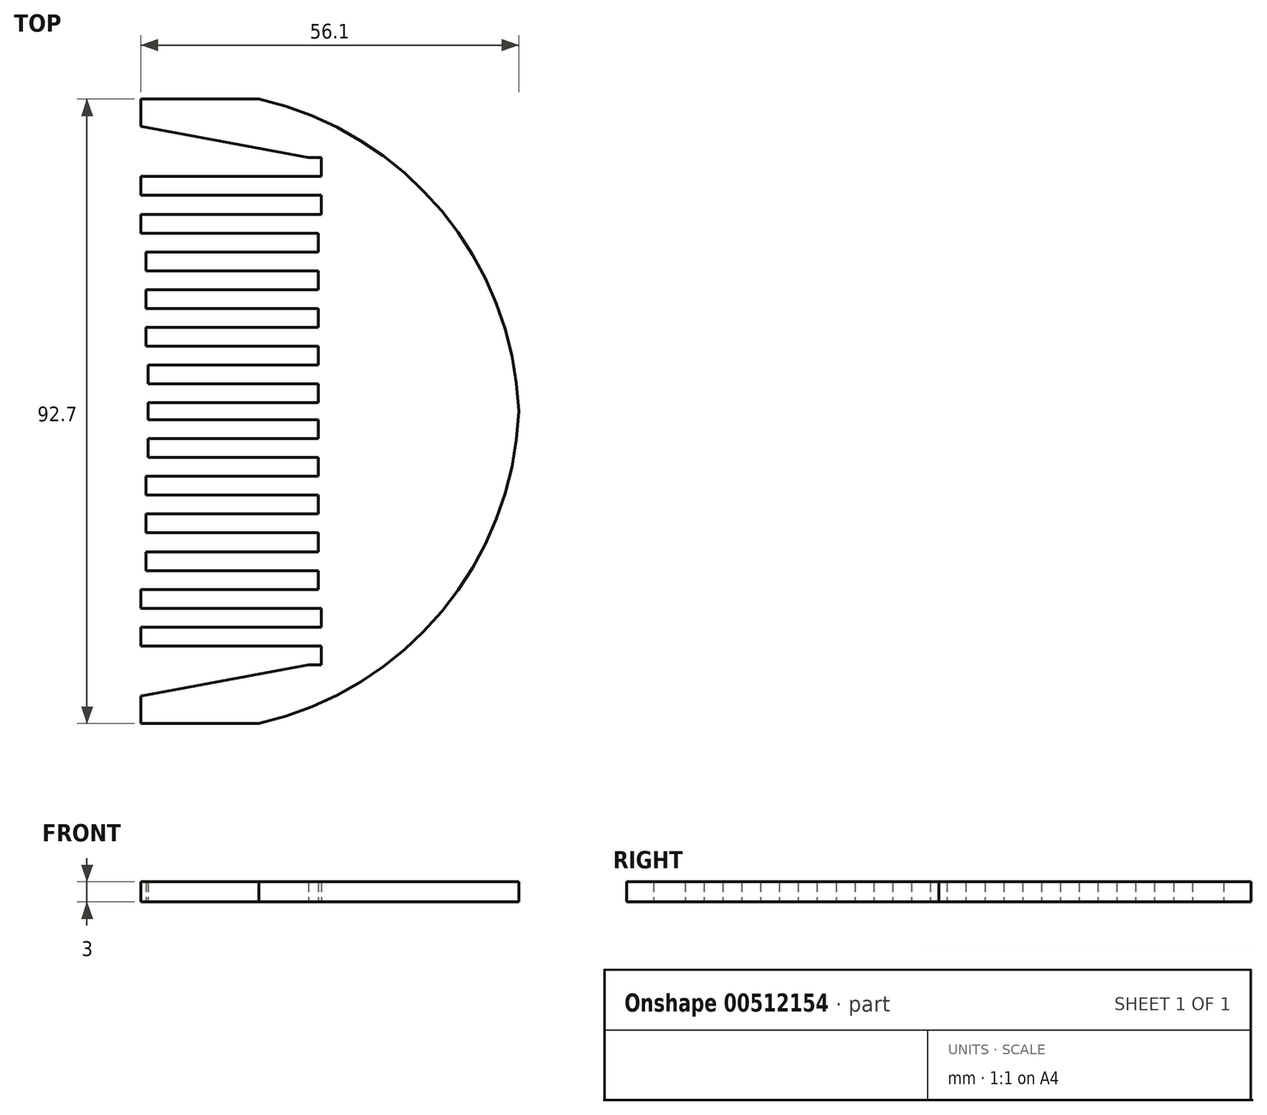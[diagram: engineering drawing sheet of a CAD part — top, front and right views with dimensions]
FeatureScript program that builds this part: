
annotation { "Feature Type Name" : "Feature", "Feature Type Description" : "" }
export const myFeature = defineFeature(function(context is Context, id is Id, definition is map)
    precondition{}
    {
        {
            var Q0;
            Q0=qCreatedBy(makeId("Top.planeOp"),FACE);
            var sketch = newSketch(context, id + "F0", { "sketchPlane" : qUnion([Q0])});
            skLineSegment(sketch, "E0", {"start": v(-57.4, 0) * mm, "end": v(-57.4, -4.05) * mm});
            skLineSegment(sketch, "E1", {"start": v(-57.4, -4.05) * mm, "end": v(-32.5, -8.7) * mm});
            skLineSegment(sketch, "E2", {"start": v(-32.5, -8.7) * mm, "end": v(-30.6, -8.7) * mm});
            skLineSegment(sketch, "E3", {"start": v(-30.6, -8.7) * mm, "end": v(-30.6, -11.5) * mm});
            skLineSegment(sketch, "E4", {"start": v(-30.6, -11.5) * mm, "end": v(-57.4, -11.5) * mm});
            skLineSegment(sketch, "E5", {"start": v(-57.4, -11.5) * mm, "end": v(-57.4, -14.3) * mm});
            skLineSegment(sketch, "E6", {"start": v(-57.4, -14.3) * mm, "end": v(-30.6, -14.3) * mm});
            skLineSegment(sketch, "E7", {"start": v(-30.6, -14.3) * mm, "end": v(-30.6, -17.1) * mm});
            skLineSegment(sketch, "E8", {"start": v(-30.6, -17.1) * mm, "end": v(-57.4, -17.1) * mm});
            skLineSegment(sketch, "E9", {"start": v(-57.4, -17.1) * mm, "end": v(-57.4, -19.9) * mm});
            skLineSegment(sketch, "E10", {"start": v(-57.4, -19.9) * mm, "end": v(-31.06, -19.9) * mm});
            skLineSegment(sketch, "E11", {"start": v(-31.06, -19.9) * mm, "end": v(-31.06, -22.7) * mm});
            skLineSegment(sketch, "E12", {"start": v(-31.06, -22.7) * mm, "end": v(-56.63, -22.7) * mm});
            skLineSegment(sketch, "E13", {"start": v(-56.63, -22.7) * mm, "end": v(-56.63, -25.5) * mm});
            skLineSegment(sketch, "E14", {"start": v(-56.63, -25.5) * mm, "end": v(-31.06, -25.5) * mm});
            skLineSegment(sketch, "E15", {"start": v(-31.06, -25.5) * mm, "end": v(-31.06, -28.3) * mm});
            skLineSegment(sketch, "E16", {"start": v(-31.06, -28.3) * mm, "end": v(-56.63, -28.3) * mm});
            skLineSegment(sketch, "E17", {"start": v(-56.63, -28.3) * mm, "end": v(-56.63, -31.1) * mm});
            skLineSegment(sketch, "E18", {"start": v(-56.63, -31.1) * mm, "end": v(-31.06, -31.1) * mm});
            skLineSegment(sketch, "E19", {"start": v(-31.06, -31.1) * mm, "end": v(-31.06, -33.9) * mm});
            skLineSegment(sketch, "E20", {"start": v(-31.06, -33.9) * mm, "end": v(-56.63, -33.9) * mm});
            skLineSegment(sketch, "E21", {"start": v(-56.63, -33.9) * mm, "end": v(-56.63, -36.7) * mm});
            skLineSegment(sketch, "E22", {"start": v(-56.63, -36.7) * mm, "end": v(-31.06, -36.7) * mm});
            skLineSegment(sketch, "E23", {"start": v(-31.06, -36.7) * mm, "end": v(-31.06, -39.5) * mm});
            skLineSegment(sketch, "E24", {"start": v(-31.06, -39.5) * mm, "end": v(-56.34, -39.5) * mm});
            skLineSegment(sketch, "E25", {"start": v(-56.34, -39.5) * mm, "end": v(-56.34, -42.3) * mm});
            skLineSegment(sketch, "E26", {"start": v(-56.34, -42.3) * mm, "end": v(-31.06, -42.3) * mm});
            skLineSegment(sketch, "E27", {"start": v(-31.06, -42.3) * mm, "end": v(-31.06, -45.1) * mm});
            skLineSegment(sketch, "E28", {"start": v(-31.06, -45.1) * mm, "end": v(-56.34, -45.1) * mm});
            skLineSegment(sketch, "E29", {"start": v(-56.34, -45.1) * mm, "end": v(-56.34, -46.35) * mm});
            skLineSegment(sketch, "E30", {"start": v(-56.34, -46.35) * mm, "end": v(-1.3, -46.35) * mm, "construction": true});
            skLineSegment(sketch, "E31", {"start": v(-57.4, 0) * mm, "end": v(-39.9, 0) * mm});
            skArc(sketch, "E32", {"start": v(-1.3, -46.35) * mm, "mid": v(-12.74, -16.63) * mm, "end": v(-39.9, 0) * mm});
            skLineSegment(sketch, "E33.MirrorCS", {"start": v(-57.4, -92.7) * mm, "end": v(-57.4, -88.66) * mm});
            skLineSegment(sketch, "E34.MirrorCS", {"start": v(-56.34, -47.6) * mm, "end": v(-56.34, -46.35) * mm});
            skLineSegment(sketch, "E35.MirrorCS", {"start": v(-56.63, -70) * mm, "end": v(-56.63, -67.2) * mm});
            skLineSegment(sketch, "E36.MirrorCS", {"start": v(-30.6, -78.4) * mm, "end": v(-30.6, -75.6) * mm});
            skLineSegment(sketch, "E37.MirrorCS", {"start": v(-31.06, -67.2) * mm, "end": v(-31.06, -64.4) * mm});
            skLineSegment(sketch, "E38.MirrorCS", {"start": v(-56.63, -64.4) * mm, "end": v(-56.63, -61.6) * mm});
            skLineSegment(sketch, "E39.MirrorCS", {"start": v(-56.34, -53.2) * mm, "end": v(-56.34, -50.4) * mm});
            skLineSegment(sketch, "E40.MirrorCS", {"start": v(-56.63, -58.8) * mm, "end": v(-56.63, -56) * mm});
            skLineSegment(sketch, "E41.MirrorCS", {"start": v(-31.06, -61.6) * mm, "end": v(-31.06, -58.8) * mm});
            skLineSegment(sketch, "E42.MirrorCS", {"start": v(-31.06, -56) * mm, "end": v(-31.06, -53.2) * mm});
            skLineSegment(sketch, "E43.MirrorCS", {"start": v(-32.5, -84) * mm, "end": v(-30.6, -84) * mm});
            skLineSegment(sketch, "E44.MirrorCS", {"start": v(-57.4, -81.2) * mm, "end": v(-57.4, -78.4) * mm});
            skLineSegment(sketch, "E45.MirrorCS", {"start": v(-31.06, -50.4) * mm, "end": v(-31.06, -47.6) * mm});
            skLineSegment(sketch, "E46.MirrorCS", {"start": v(-30.6, -84) * mm, "end": v(-30.6, -81.2) * mm});
            skLineSegment(sketch, "E47.MirrorCS", {"start": v(-57.4, -75.6) * mm, "end": v(-57.4, -72.8) * mm});
            skLineSegment(sketch, "E48.MirrorCS", {"start": v(-31.06, -72.8) * mm, "end": v(-31.06, -70) * mm});
            skLineSegment(sketch, "E49.MirrorCS", {"start": v(-57.4, -72.8) * mm, "end": v(-31.06, -72.8) * mm});
            skLineSegment(sketch, "E50.MirrorCS", {"start": v(-56.63, -56) * mm, "end": v(-31.06, -56) * mm});
            skLineSegment(sketch, "E51.MirrorCS", {"start": v(-57.4, -88.66) * mm, "end": v(-32.5, -84) * mm});
            skLineSegment(sketch, "E52.MirrorCS", {"start": v(-31.06, -47.6) * mm, "end": v(-56.34, -47.6) * mm});
            skLineSegment(sketch, "E53.MirrorCS", {"start": v(-56.34, -50.4) * mm, "end": v(-31.06, -50.4) * mm});
            skArc(sketch, "E54.MirrorCS", {"start": v(-1.3, -46.35) * mm, "mid": v(-12.74, -76.07) * mm, "end": v(-39.9, -92.7) * mm});
            skLineSegment(sketch, "E55.MirrorCS", {"start": v(-57.4, -92.7) * mm, "end": v(-39.9, -92.7) * mm});
            skLineSegment(sketch, "E56.MirrorCS", {"start": v(-30.6, -81.2) * mm, "end": v(-57.4, -81.2) * mm});
            skLineSegment(sketch, "E57.MirrorCS", {"start": v(-56.63, -67.2) * mm, "end": v(-31.06, -67.2) * mm});
            skLineSegment(sketch, "E58.MirrorCS", {"start": v(-31.06, -53.2) * mm, "end": v(-56.34, -53.2) * mm});
            skLineSegment(sketch, "E59.MirrorCS", {"start": v(-31.06, -64.4) * mm, "end": v(-56.63, -64.4) * mm});
            skLineSegment(sketch, "E60.MirrorCS", {"start": v(-56.63, -61.6) * mm, "end": v(-31.06, -61.6) * mm});
            skLineSegment(sketch, "E61.MirrorCS", {"start": v(-31.06, -58.8) * mm, "end": v(-56.63, -58.8) * mm});
            skLineSegment(sketch, "E62.MirrorCS", {"start": v(-30.6, -75.6) * mm, "end": v(-57.4, -75.6) * mm});
            skLineSegment(sketch, "E63.MirrorCS", {"start": v(-31.06, -70) * mm, "end": v(-56.63, -70) * mm});
            skLineSegment(sketch, "E64.MirrorCS", {"start": v(-57.4, -78.4) * mm, "end": v(-30.6, -78.4) * mm});
            skSolve(sketch);
        }
        {
            var Q0;
            Q0=makeQuery(id+"F0.imprint","IMPRINT",FACE,{"disambiguationData":[TD([[makeQuery(id+"F0.imprint","IMPRINT",EDGE,{"derivedFrom":sQuery(id+"F0.wireOp",EDGE,"E0")}),1.0]])]});
            extrude(context, id + "F1", {"entities" : qUnion([Q0]), "depth" : 3 * mm});
        }
    });
